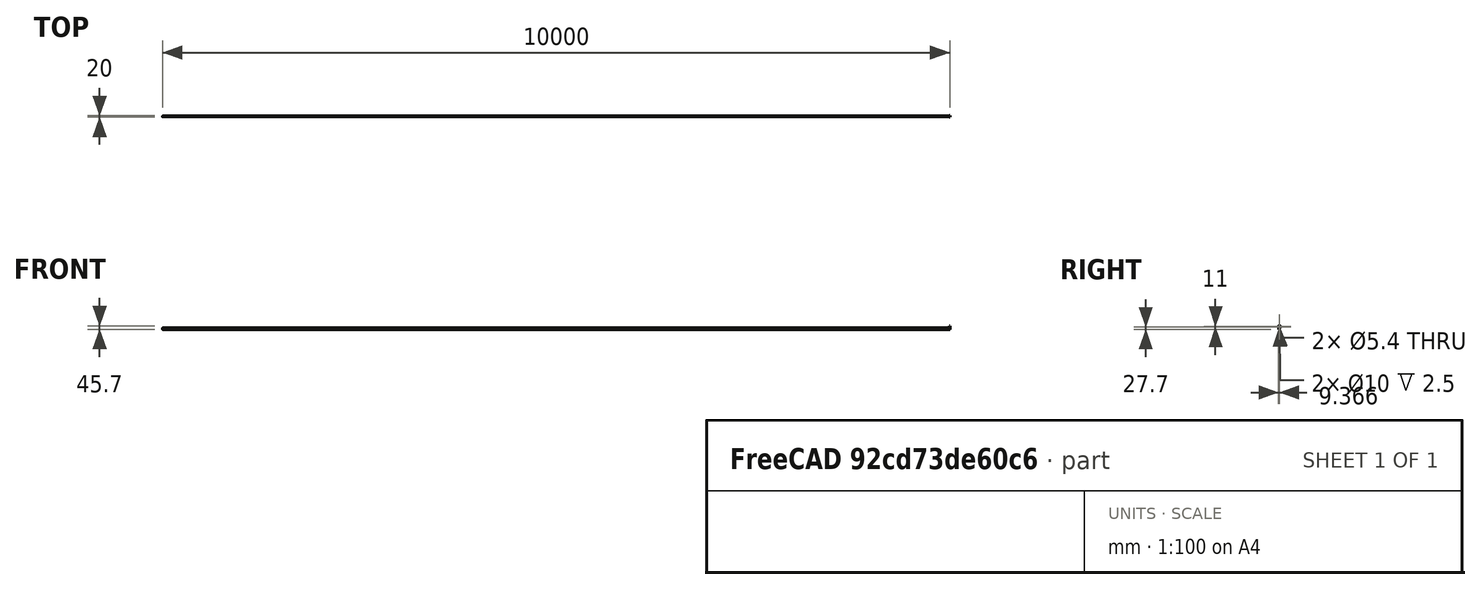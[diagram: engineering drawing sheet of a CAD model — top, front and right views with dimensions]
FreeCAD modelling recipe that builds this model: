
FCSTD DOCUMENT  (FreeCAD 0.16R)
Label: RackHookNutfcstd
License: All rights reserved
LicenseURL: http://en.wikipedia.org/wiki/All_rights_reserved
objects: Sketcher::SketchObject×3, PartDesign::Pocket×2, PartDesign::Fillet×2, PartDesign::Pad×1, Mesh::Feature×1
note: 11 computed .brp shape members not serialized (recipe doc carries the construction recipe); baked Part::Feature solids carry a one-line shape summary decoded from their .brp

FEATURE [Sketcher::SketchObject] Sketch002
  Placement = pos=(0,0,25) rot=(0,0,1;0rad)
  sketch-geometry (4):
    g0: LineSegment StartX=3.82476 StartY=-14.7416 StartZ=0 EndX=8.82476 EndY=-14.7416 EndZ=0
    g1: LineSegment StartX=8.82476 StartY=-14.7416 StartZ=0 EndX=8.82476 EndY=-34.7416 EndZ=0
    g2: LineSegment StartX=8.82476 StartY=-34.7416 StartZ=0 EndX=3.82476 EndY=-34.7416 EndZ=0
    g3: LineSegment StartX=3.82476 StartY=-34.7416 StartZ=0 EndX=3.82476 EndY=-14.7416 EndZ=0
  constraints (10):
    c: Coincident(g0,g1)
    c: Coincident(g1,g2)
    c: Coincident(g2,g3)
    c: Coincident(g3,g0)
    c: Horizontal(g0)
    c: Horizontal(g2)
    c: Vertical(g1)
    c: Vertical(g3)
    c: Distance(g2) = 5
    c: Distance(g1) = 20
FEATURE [PartDesign::Pad] Pad
  Length = 25
  Length2 = 100
  Placement = pos=(0,0,25) rot=(0,0,1;0rad)
  Sketch = -> Sketch002
  Type = 0
FEATURE [Sketcher::SketchObject] Sketch006
  Placement = pos=(8.82476,0,25) rot=(0.57735,0.57735,0.57735;2.0944rad)
  Support = -> Pad [Face2]
  sketch-geometry (2):
    g0: Circle CenterX=-25.3745 CenterY=7 CenterZ=0 NormalX=0 NormalY=0 NormalZ=1 Radius=2.7
    g1: Circle CenterX=-25.3745 CenterY=18 CenterZ=0 NormalX=0 NormalY=0 NormalZ=1 Radius=2.7
  constraints (5):
    c: Radius(g0) = 2.7
    c: Equal(g0,g1)
    c: Distance(g0,g1) = 11
    c: DistanceX(g0,g1) = 0
    c: DistanceY(g0) = 7
FEATURE [PartDesign::Pocket] Pocket
  Length = 5
  Placement = pos=(0,0,25) rot=(0,0,1;0rad)
  Sketch = -> Sketch006
  Type = 1
FEATURE [Sketcher::SketchObject] Sketch
  ExternalGeometry = -> [Pocket]
  Placement = pos=(3.82476,0,25) rot=(0.57735,-0.57735,-0.57735;2.0944rad)
  Support = -> Pocket [Face2]
  sketch-geometry (2):
    g0: Circle CenterX=25.3745 CenterY=18 CenterZ=0 NormalX=0 NormalY=0 NormalZ=1 Radius=5
    g1: Circle CenterX=25.3745 CenterY=7 CenterZ=0 NormalX=0 NormalY=0 NormalZ=1 Radius=5
  constraints (4):
    c: Radius(g0) = 5
    c: Equal(g0,g1)
    c: Coincident(g1,g-4)
    c: Coincident(g0,g-3)
FEATURE [PartDesign::Pocket] Pocket001
  Length = 2.5
  Placement = pos=(0,0,25) rot=(0,0,1;0rad)
  Sketch = -> Sketch
  Type = 0
FEATURE [PartDesign::Fillet] Fillet
  Base = -> Pocket001 [Edge3,Edge15,Edge16,Edge4]
  Placement = pos=(0,0,25) rot=(0,0,1;0rad)
  Radius = 2
FEATURE [PartDesign::Fillet] Fillet001
  Base = -> Fillet [Edge1]
  Placement = pos=(0,0,25) rot=(0,0,1;0rad)
  Radius = 1
FEATURE [Mesh::Feature] Mesh  label="Fillet001 (Meshed)"
